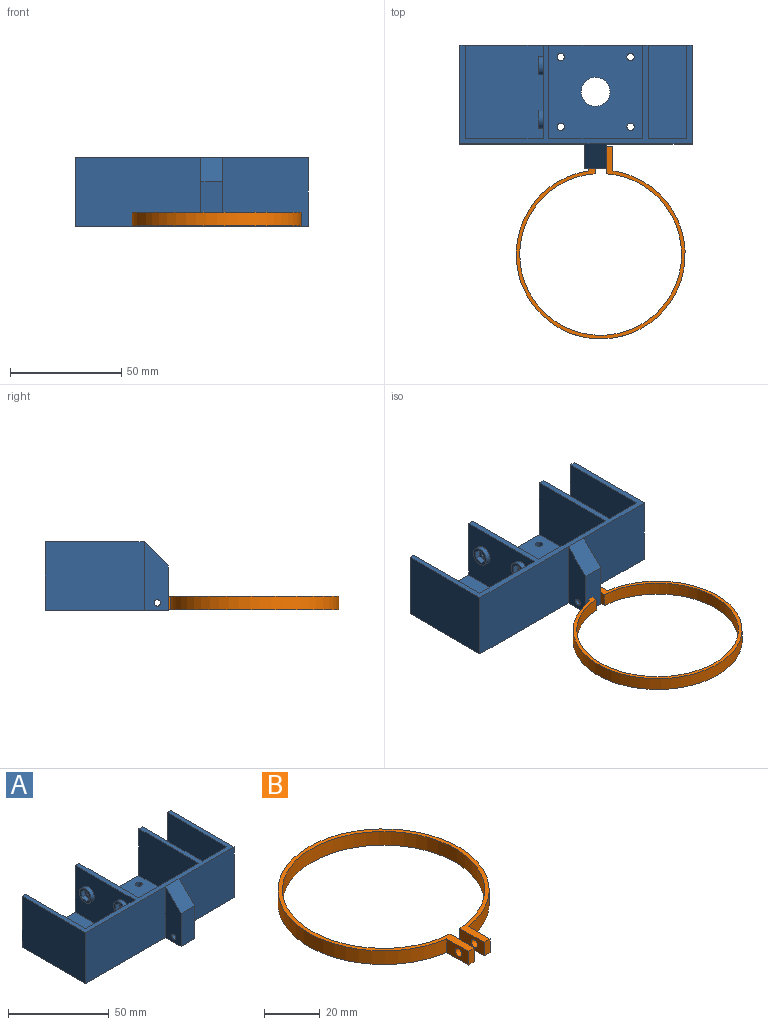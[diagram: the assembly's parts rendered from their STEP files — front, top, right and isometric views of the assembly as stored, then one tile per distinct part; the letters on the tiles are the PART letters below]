
ASSEMBLY  parts=2 mates=1
PART A: 49 faces, bbox 104.6x55.5x31 mm
  f0: cylinder r=1.65mm len=3.3mm, axis (-1,0,0), area 24.9mm2, adj f23,f35
  f1: plane 8.3x8.3mm, normal (-1,0,0), area 28.9mm2, adj f33,f42,f43,f44,f45,f46,f47
  f2: plane 8.3x8.3mm, normal (-1,0,0), area 28.9mm2, adj f34,f36,f37,f38,f39,f40,f41
  f3: plane 42x28.5mm, normal (-1,0,0), area 1088.8mm2, adj f5,f14,f16,f25,f33,f34
  f4: plane 42x17.35mm, normal (0,0,1), area 728.7mm2, adj f14,f27,f29,f31
  f5: plane 35x28.5mm, normal (0,1,0), area 997.5mm2, adj f3,f16,f25,f26
  f6: plane 42.2x42mm, normal (0,0,1), area 1605.5mm2, adj f9,f10,f11,f12,f13,f14,f17,f23
  f7: plane 38.65x31mm, normal (0,-1,0), area 1198.2mm2, adj f15,f16,f18,f30
  f8: plane 56.3x31mm, normal (0,-1,0), area 1745.3mm2, adj f15,f16,f19,f24
  f9: cylinder r=6.5mm len=13mm, axis (0,0,-1), area 102.1mm2, adj f6,f15
  f10: cylinder r=1.65mm len=3.3mm, axis (0,0,-1), area 25.9mm2, adj f6,f15
  f11: cylinder r=1.65mm len=3.3mm, axis (0,0,-1), area 25.9mm2, adj f6,f15
  f12: cylinder r=1.65mm len=3.3mm, axis (0,0,-1), area 25.9mm2, adj f6,f15
  f13: cylinder r=1.65mm len=3.3mm, axis (0,0,-1), area 25.9mm2, adj f6,f15
  f14: plane 104.55x31mm, normal (0,1,0), area 546.4mm2, adj f3,f4,f6,f15,f16,f23,f24,f25
  f15: plane 104.55x55.5mm, normal (0,0,-1), area 4591.1mm2, adj f7,f8,f9,f10,f11,f12,f13,f14
  f16: plane 104.55x44.5mm, normal (0,0,1), area 681.4mm2, adj f3,f5,f7,f8,f14,f17,f22,f23
  f17: plane 42.2x28.5mm, normal (0,1,0), area 1202.7mm2, adj f6,f16,f23,f28
  f18: plane 31x11mm, normal (1,0,0), area 273.8mm2, adj f7,f15,f20,f21,f22
  f19: plane 31x11mm, normal (-1,0,0), area 273.8mm2, adj f8,f15,f20,f21,f22
  f20: plane 20x9.6mm, normal (0,-1,0), area 192mm2, adj f15,f18,f19,f22
  f21: cylinder r=1.46mm len=9.6mm, axis (-1,0,0), area 87.9mm2, adj f18,f19
  f22: plane 11x11mm, normal (0,-0.71,0.71), area 149.3mm2, adj f16,f18,f19,f20
  f23: plane 42x28.5mm, normal (1,0,0), area 1179.9mm2, adj f0,f6,f14,f16,f17,f32
  f24: plane 44.5x31mm, normal (-1,0,0), area 1379.5mm2, adj f8,f14,f15,f16
  f25: plane 42x35mm, normal (0,0,1), area 1470mm2, adj f3,f5,f14,f26
  f26: plane 42x28.5mm, normal (1,0,0), area 1197mm2, adj f5,f14,f16,f25
  f27: plane 42x28.5mm, normal (1,0,0), area 1197mm2, adj f4,f14,f16,f29
  f28: plane 42x28.5mm, normal (-1,0,0), area 1197mm2, adj f6,f14,f16,f17
  f29: plane 28.5x17.35mm, normal (0,1,0), area 494.5mm2, adj f4,f16,f27,f31
  f30: plane 44.5x31mm, normal (1,0,0), area 1379.5mm2, adj f7,f14,f15,f16
  f31: plane 42x28.5mm, normal (-1,0,0), area 1197mm2, adj f4,f14,f16,f29
  f32: cylinder r=1.65mm len=3.3mm, axis (-1,0,0), area 24.9mm2, adj f23,f48
  f33: cylinder r=4.15mm len=8.3mm, axis (1,0,0), area 60mm2, adj f1,f3
  f34: cylinder r=4.15mm len=8.3mm, axis (1,0,0), area 60mm2, adj f2,f3
  f35: plane 6.17x5.79mm, normal (-1,0,0), area 16.7mm2, adj f0,f36,f37,f38,f39,f40,f41
  f36: plane 2.45x2.4mm, normal (0,-0.62,-0.79), area 7.5mm2, adj f2,f35,f37,f41
  f37: plane 3.09x2.4mm, normal (0,-0.99,0.14), area 7.5mm2, adj f2,f35,f36,f38
  f38: plane 2.9x2.4mm, normal (0,-0.37,0.93), area 7.5mm2, adj f2,f35,f37,f39
  f39: plane 2.45x2.4mm, normal (0,0.62,0.79), area 7.5mm2, adj f2,f35,f38,f40
  f40: plane 3.09x2.4mm, normal (0,0.99,-0.14), area 7.5mm2, adj f2,f35,f39,f41
  f41: plane 2.9x2.4mm, normal (0,0.37,-0.93), area 7.5mm2, adj f2,f35,f36,f40
  f42: plane 2.4x2.33mm, normal (0,-0.66,-0.75), area 7.5mm2, adj f1,f43,f47,f48
  f43: plane 3.05x2.4mm, normal (0,-0.98,0.2), area 7.5mm2, adj f1,f42,f44,f48
  f44: plane 2.96x2.4mm, normal (0,-0.32,0.95), area 7.5mm2, adj f1,f43,f45,f48
  f45: plane 2.4x2.33mm, normal (0,0.66,0.75), area 7.5mm2, adj f1,f44,f46,f48
  f46: plane 3.05x2.4mm, normal (0,0.98,-0.2), area 7.5mm2, adj f1,f45,f47,f48
  f47: plane 2.96x2.4mm, normal (0,0.32,-0.95), area 7.5mm2, adj f1,f42,f46,f48
  f48: plane 6.11x5.92mm, normal (-1,0,0), area 16.7mm2, adj f32,f42,f43,f44,f45,f46,f47
PART B: 12 faces, bbox 76x86.7x6 mm
  f0: cylinder r=38mm len=76mm, axis (0,0,-1), area 1366.3mm2, adj f3,f4,f6,f9
  f1: plane 12.34x6mm, normal (1,0,0), area 65.5mm2, adj f3,f4,f5,f7,f8
  f2: plane 12.33x6mm, normal (-1,0,0), area 65.5mm2, adj f3,f4,f5,f10,f11
  f3: plane 86.65x76mm, normal (0,0,1), area 431.2mm2, adj f0,f1,f2,f5,f6,f8,f9,f11
  f4: plane 86.65x76mm, normal (0,0,-1), area 431.2mm2, adj f0,f1,f2,f5,f6,f8,f9,f11
  f5: cylinder r=36.4mm len=72.8mm, axis (0,0,1), area 1342.2mm2, adj f1,f2,f3,f4
  f6: plane 11.05x6mm, normal (-1,0,0), area 57.8mm2, adj f0,f3,f4,f7,f8
  f7: cylinder r=1.65mm len=3.3mm, axis (1,0,0), area 31.1mm2, adj f1,f6
  f8: plane 6x3mm, normal (0,-1,0), area 18mm2, adj f1,f3,f4,f6
  f9: plane 11.05x6mm, normal (1,0,0), area 57.7mm2, adj f0,f3,f4,f10,f11
  f10: cylinder r=1.65mm len=3.3mm, axis (-1,0,0), area 31.1mm2, adj f2,f9
  f11: plane 6x3mm, normal (0,-1,0), area 18mm2, adj f2,f3,f4,f9
PLACE A t=(63.31,32.92,38.98)mm
PLACE B rot(axis=(0,0,-1),180deg) t=(63.45,-5.99,39.4)mm
MATE fastened A.f21 <-> B.f10  axis (1,0,0) through (65.98,37.66,42.4)mm
